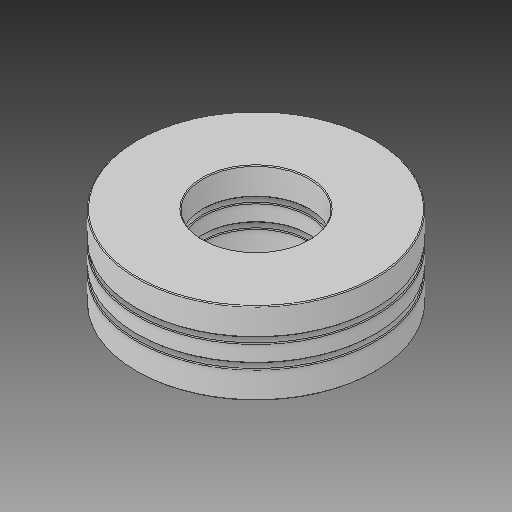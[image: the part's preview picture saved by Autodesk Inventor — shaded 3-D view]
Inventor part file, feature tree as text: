
AUTODESK INVENTOR PART (.ipt)
format: ipt  version: 2019 (Build 230136000, 136)  size: 507,392 bytes
history: native  units: in
note: dims shown in document units (in); Inventor stores cm internally (conversion verified against a paired STEP export)
features: other x6, fillet x3, revolve x1
ambient origin geometry x8: Origin, YZ Plane, XZ Plane, XY Plane, X Axis, Y Axis, Z Axis, Center Point
bodies: Solid1 (feature_tree), Solid2 (feature_tree), Solid3 (feature_tree), Solid4 (feature_tree), Solid5 (feature_tree), Solid6 (feature_tree), Solid7 (feature_tree), Solid8 (feature_tree), Solid9 (feature_tree), Solid10 (feature_tree)
feature tree (10):
  revolve  "Revolve2"  [1 undecoded]
  other  "CirPattern1[1]"
  other  "CirPattern1[2]"
  other  "CirPattern1[3]"
  other  "CirPattern1[4]"
  other  "CirPattern1[5]"
  other  "CirPattern1[6]"
  fillet  "Fillet2"  [1 undecoded]
  fillet  "Fillet1"  [1 undecoded]
  fillet  "Fillet3"  [1 undecoded]
note: 4 required parameter values undecoded (feature->parameter linkage not recoverable at this tier; creation-order binding heuristic only, values carry confidence <= 0.55)
